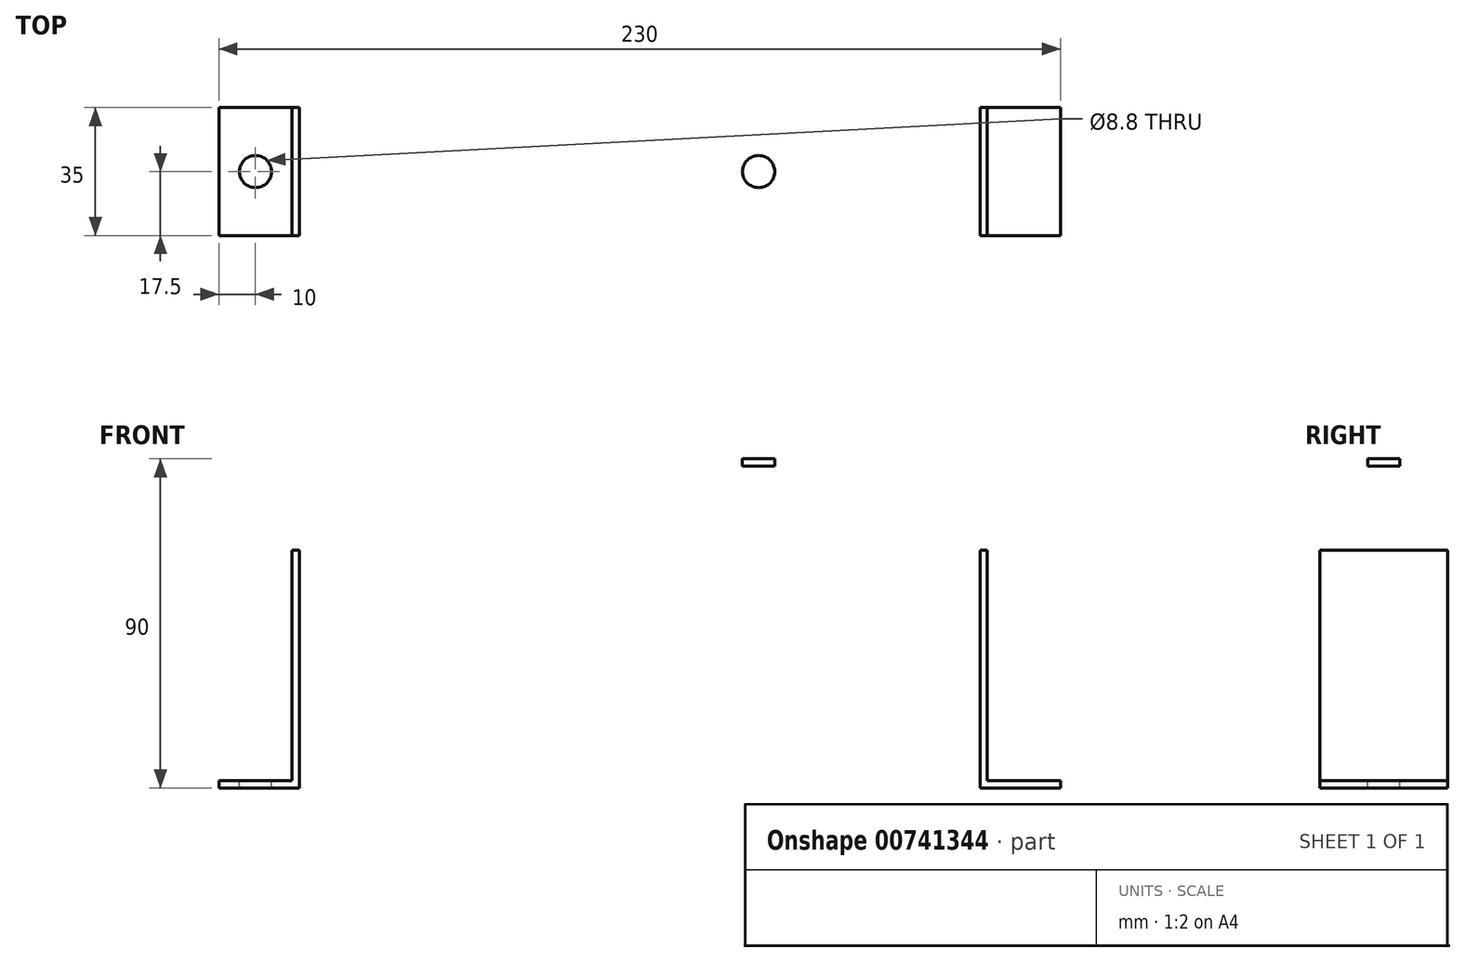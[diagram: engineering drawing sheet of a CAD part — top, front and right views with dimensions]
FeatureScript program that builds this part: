
annotation { "Feature Type Name" : "Feature", "Feature Type Description" : "" }
export const myFeature = defineFeature(function(context is Context, id is Id, definition is map)
    precondition{}
    {
        {
            var Q0;
            Q0=qCreatedBy(makeId("Front.planeOp"),FACE);
            var sketch = newSketch(context, id + "F0", { "sketchPlane" : qUnion([Q0])});
            skLineSegment(sketch, "E0.bottom", {"start": v(95, 50) * mm, "end": v(-95, 50) * mm});
            skLineSegment(sketch, "E0.left", {"start": v(95, 50) * mm, "end": v(95, -38) * mm});
            skLineSegment(sketch, "E0.right", {"start": v(-95, 50) * mm, "end": v(-95, -38) * mm});
            skLineSegment(sketch, "E1.bottom", {"start": v(-93, -40) * mm, "end": v(-115, -40) * mm});
            skLineSegment(sketch, "E1.top", {"start": v(-95, -38) * mm, "end": v(-115, -38) * mm});
            skLineSegment(sketch, "E1.right", {"start": v(-115, -40) * mm, "end": v(-115, -38) * mm});
            skLineSegment(sketch, "E2.MirrorCS", {"start": v(95, -38) * mm, "end": v(115, -38) * mm});
            skLineSegment(sketch, "E3.MirrorCS", {"start": v(115, -40) * mm, "end": v(115, -38) * mm});
            skLineSegment(sketch, "E4.MirrorCS", {"start": v(93, -40) * mm, "end": v(115, -40) * mm});
            skLineSegment(sketch, "E5.bottom", {"start": v(93, 48) * mm, "end": v(-93, 48) * mm});
            skLineSegment(sketch, "E5.left", {"start": v(93, 48) * mm, "end": v(93, -40) * mm});
            skLineSegment(sketch, "E5.right", {"start": v(-93, 48) * mm, "end": v(-93, -40) * mm});
            skPoint(sketch, "E5.middle", {"position": v(0, 0) * mm});
            skSolve(sketch);
        }
        {
            var Q0;
            Q0=makeQuery(id+"F0.imprint","IMPRINT",FACE,{"disambiguationData":[TD([[makeQuery(id+"F0.imprint","IMPRINT",EDGE,{"derivedFrom":sQuery(id+"F0.wireOp",EDGE,"KYryMLYI-daS0-5E23-TXuT-T7hqRafUo6E8.bottom")}),1.0]])]});
            var Q1;
            Q1=makeQuery(id+"F0.imprint","IMPRINT",FACE,{"disambiguationData":[TD([[makeQuery(id+"F0.imprint","IMPRINT",EDGE,{"derivedFrom":sQuery(id+"F0.wireOp",EDGE,"E0.bottom")}),1.0]])]});
            extrude(context, id + "F1", {"entities" : qUnion([Q0, Q1]), "endBound" : BoundingType.SYMMETRIC, "depth" : 35 * mm, "offsetDistance" : 25 * mm});
        }
        {
            var Q0;
            Q0=makeQuery(id+"F1.opExtrude","SWEPT_FACE",FACE,{"disambiguationData":[OSD([sQuery(id+"F0.wireOp",EDGE,"E1.top")])]});
            var sketch = newSketch(context, id + "F2", { "sketchPlane" : qUnion([Q0])});
            skCircle(sketch, "E6", {"center": v(-105, 0) * mm, "radius": 4.4 * mm});
            skPoint(sketch, "E6.centerSnap0", {"position": v(-105, -17.5) * mm});
            skPoint(sketch, "E6.centerSnap1", {"position": v(-115, 0) * mm});
            skCircle(sketch, "E7.MirrorC", {"center": v(105, 0) * mm, "radius": 4.4 * mm});
            skSolve(sketch);
        }
        {
            var Q0;
            Q0=makeQuery(id+"F2.imprint","IMPRINT",FACE,{"disambiguationData":[TD([[makeQuery(id+"F2.imprint","IMPRINT",EDGE,{"derivedFrom":sQuery(id+"F2.wireOp",EDGE,"E6")}),1.0]])]});
            var Q1;
            Q1=makeQuery(id+"F2.imprint","IMPRINT",FACE,{"disambiguationData":[TD([[makeQuery(id+"F2.imprint","IMPRINT",EDGE,{"derivedFrom":sQuery(id+"F2.wireOp",EDGE,"E7.MirrorC")}),-1.0]])]});
            extrude(context, id + "F3", {"entities" : qUnion([Q0, Q1]), "operationType" : NewBodyOperationType.REMOVE, "oppositeDirection" : true, "depth" : 25 * mm, "offsetDistance" : 25 * mm});
        }
        {
            var Q0;
            Q0=makeQuery(id+"F1.opExtrude","SWEPT_FACE",FACE,{"disambiguationData":[OSD([sQuery(id+"F0.wireOp",EDGE,"E0.bottom")])]});
            var sketch = newSketch(context, id + "F4", { "sketchPlane" : qUnion([Q0])});
            skCircle(sketch, "E8", {"center": v(-32.5, 0) * mm, "radius": 4.4 * mm});
            skCircle(sketch, "E9.MirrorC", {"center": v(32.5, 0) * mm, "radius": 4.4 * mm});
            skSolve(sketch);
        }
        {
            var Q0;
            Q0=makeQuery(id+"F4.imprint","IMPRINT",FACE,{"disambiguationData":[TD([[makeQuery(id+"F4.imprint","IMPRINT",EDGE,{"derivedFrom":sQuery(id+"F4.wireOp",EDGE,"E8")}),1.0]])]});
            var Q1;
            Q1=makeQuery(id+"F4.imprint","IMPRINT",FACE,{"disambiguationData":[TD([[makeQuery(id+"F4.imprint","IMPRINT",EDGE,{"derivedFrom":sQuery(id+"F4.wireOp",EDGE,"E9.MirrorC")}),-1.0]])]});
            extrude(context, id + "F5", {"entities" : qUnion([Q0, Q1]), "operationType" : NewBodyOperationType.REMOVE, "oppositeDirection" : true, "depth" : 25 * mm, "offsetDistance" : 25 * mm});
        }
    });
